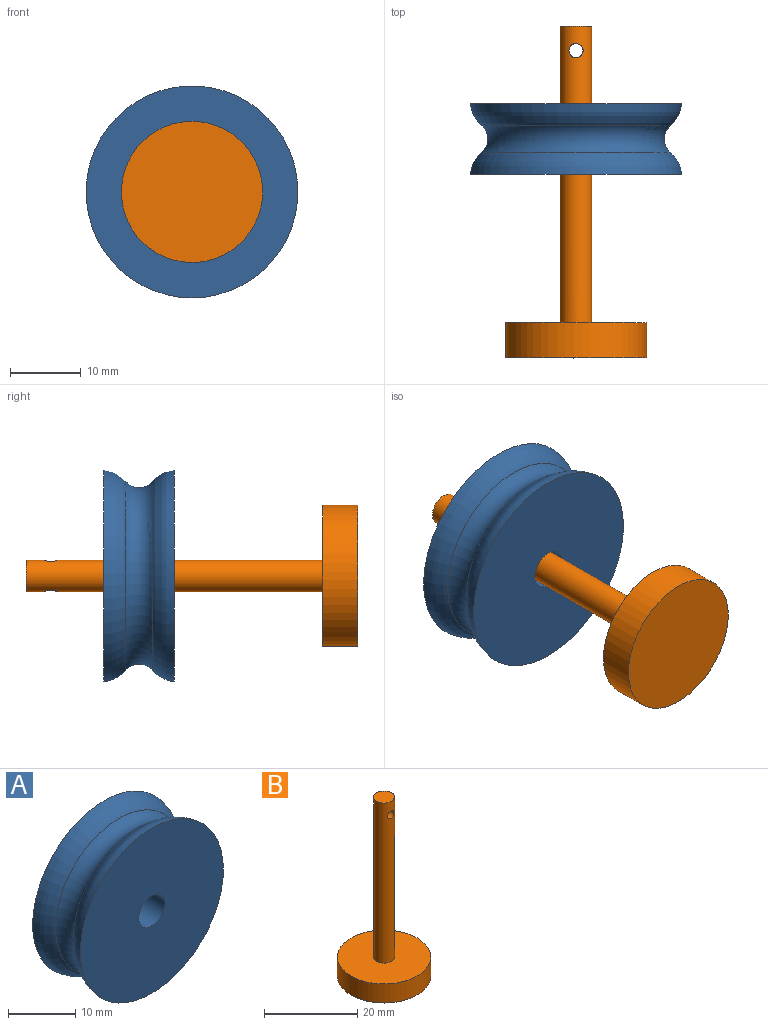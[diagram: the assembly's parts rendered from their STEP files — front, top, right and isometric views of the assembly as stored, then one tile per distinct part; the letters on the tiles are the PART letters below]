
ASSEMBLY  parts=2 mates=1
PART A: 6 faces, bbox 32.6x11.3x32.6 mm
  f0: plane 30x30mm, normal (0,-1,0), area 683.1mm2, adj f3,f5
  f1: torus R=15mm, axis (0,-1,0), area 340.7mm2, adj f3,f4
  f2: plane 30x30mm, normal (0,1,0), area 683.1mm2, adj f4,f5
  f3: torus R=10.04mm, axis (0,1,0), area 326.1mm2, adj f0,f1
  f4: torus R=10.04mm, axis (0,-1,0), area 326.1mm2, adj f1,f2
  f5: cylinder r=2.75mm len=10mm, axis (0,-1,0), area 172.8mm2, adj f0,f2
PART B: 6 faces, bbox 20x20x47 mm
  f0: cylinder r=10mm len=20mm, axis (0,0,-1), area 314.2mm2, adj f1,f2
  f1: plane 20x20mm, normal (0,0,1), area 298.3mm2, adj f0,f3
  f2: plane 20x20mm, normal (0,0,-1), area 314.2mm2, adj f0
  f3: cylinder r=2.25mm len=42mm, axis (0,0,-1), area 587.3mm2, adj f1,f4,f5
  f4: plane 4.5x4.5mm, normal (0,0,1), area 15.9mm2, adj f3
  f5: cylinder r=1mm len=4.5mm, axis (0,-1,0), area 26.8mm2, adj f3
PLACE A t=(-33.89,-3.77,23.7)mm
PLACE B rot(axis=(-1,0,0),90deg) t=(-33.89,-34.77,23.7)mm
MATE fastened B.f3 <-> A.f3  axis (0,-1,0) through (-33.89,-8.77,23.7)mm
